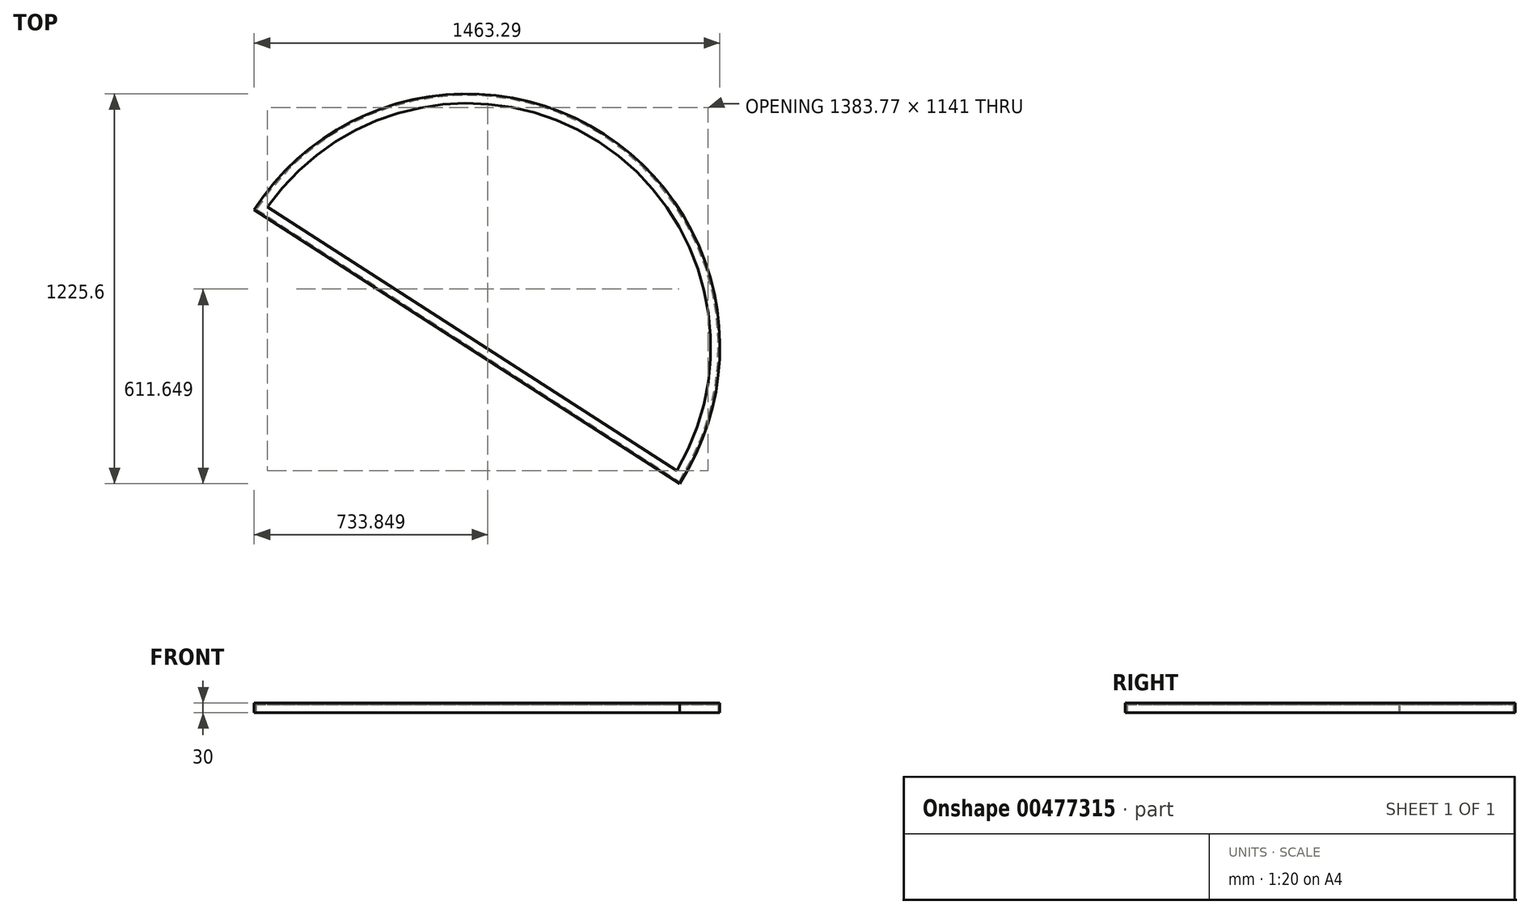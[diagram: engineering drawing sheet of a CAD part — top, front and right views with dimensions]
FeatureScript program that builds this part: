
annotation { "Feature Type Name" : "Feature", "Feature Type Description" : "" }
export const myFeature = defineFeature(function(context is Context, id is Id, definition is map)
    precondition{}
    {
        {
            var Q0;
            Q0=qCreatedBy(makeId("Top.planeOp"),FACE);
            var sketch = newSketch(context, id + "F0", { "sketchPlane" : qUnion([Q0])});
            skArc(sketch, "E0", {"start": v(668.29, -430.6) * mm, "mid": v(430.6, 668.29) * mm, "end": v(-668.29, 430.6) * mm});
            skArc(sketch, "E1", {"start": v(664.09, -427.9) * mm, "mid": v(427.9, 664.09) * mm, "end": v(-664.09, 427.9) * mm});
            skLineSegment(sketch, "E2", {"start": v(-668.29, 430.6) * mm, "end": v(0, 0) * mm});
            skLineSegment(sketch, "E3", {"start": v(0, 0) * mm, "end": v(668.29, -430.6) * mm});
            skLineSegment(sketch, "E4", {"start": v(-664.09, 433.84) * mm, "end": v(668.29, -424.65) * mm});
            skSolve(sketch);
        }
        {
            var Q0;
            Q0=makeQuery(id+"F0.imprint","IMPRINT",FACE,{"disambiguationData":[TD([[makeQuery(id+"F0.imprint","IMPRINT",EDGE,{"derivedFrom":sQuery(id+"F0.wireOp",EDGE,"E0")}),1.0]])]});
            var Q1;
            {var subQ1=sQuery(id+"F0.wireOp",EDGE,"E1");var subQ3=sQuery(id+"F0.wireOp",EDGE,"E3");var subQ7=makeQuery(id+"F0.imprint","INTERSECT",VERTEX,{"derivedFrom":[subQ1,subQ3]});Q1=makeQuery(id+"F0.imprint","IMPRINT",FACE,{"disambiguationData":[TD([[makeQuery(id+"F0.imprint","IMPRINT",EDGE,{"disambiguationData":[TD([[subQ7,-1.0]])],"derivedFrom":subQ1}),1.0]])]});}
            var Q2;
            {var subQ0=sQuery(id+"F0.wireOp",EDGE,"E3");var subQ1=sQuery(id+"F0.wireOp",EDGE,"E0");var subQ2=makeQuery(id+"F0.imprint","INTERSECT",VERTEX,{"derivedFrom":[subQ1,subQ0]});Q2=makeQuery(id+"F0.imprint","IMPRINT",FACE,{"disambiguationData":[TD([[makeQuery(id+"F0.imprint","IMPRINT",EDGE,{"disambiguationData":[TD([[subQ2,-1.0]])],"derivedFrom":subQ1}),1.0]])]});}
            extrude(context, id + "F1", {"entities" : qUnion([Q0, Q1, Q2]), "endBound" : BoundingType.SYMMETRIC, "oppositeDirection" : true, "depth" : 25 * mm});
        }
        {
            var Q0;
            Q0=makeQuery(id+"F1.opExtrude","CAP_FACE",FACE,{"disambiguationData":[OSD([sQuery(id+"F0.wireOp",EDGE,"E0"),sQuery(id+"F0.wireOp",EDGE,"E1"),sQuery(id+"F0.wireOp",EDGE,"E2"),sQuery(id+"F0.wireOp",EDGE,"E3"),sQuery(id+"F0.wireOp",EDGE,"E4")])],"isStart":true});
            var sketch = newSketch(context, id + "F2", { "sketchPlane" : qUnion([Q0])});
            skLineSegment(sketch, "E5.0", {"start": v(-668.29, 430.6) * mm, "end": v(668.29, -430.6) * mm});
            skArc(sketch, "E6.0", {"start": v(668.29, -430.6) * mm, "mid": v(430.6, 668.29) * mm, "end": v(-668.29, 430.6) * mm});
            skLineSegment(sketch, "E7", {"start": v(-642.99, 449.98) * mm, "end": v(670.8, -396.53) * mm});
            skSolve(sketch);
        }
        {
            var Q0;
            Q0=makeQuery(id+"F1.opExtrude","CAP_FACE",FACE,{"disambiguationData":[OSD([sQuery(id+"F0.wireOp",EDGE,"E0"),sQuery(id+"F0.wireOp",EDGE,"E1"),sQuery(id+"F0.wireOp",EDGE,"E2"),sQuery(id+"F0.wireOp",EDGE,"E3"),sQuery(id+"F0.wireOp",EDGE,"E4")])],"isStart":true});
            var sketch = newSketch(context, id + "F3", { "sketchPlane" : qUnion([Q0])});
            skArc(sketch, "E8.0", {"start": v(668.29, -430.6) * mm, "mid": v(430.6, 668.29) * mm, "end": v(-668.29, 430.6) * mm});
            skLineSegment(sketch, "E9.0", {"start": v(-668.29, 430.6) * mm, "end": v(668.29, -430.6) * mm});
            skLineSegment(sketch, "E10", {"start": v(-626.33, 439.25) * mm, "end": v(659.81, -389.45) * mm});
            skArc(sketch, "E11", {"start": v(659.81, -389.45) * mm, "mid": v(415.15, 643.23) * mm, "end": v(-626.33, 439.25) * mm});
            skSolve(sketch);
        }
        {
            var Q0;
            Q0=makeQuery(id+"F3.imprint","IMPRINT",FACE,{"disambiguationData":[TD([[makeQuery(id+"F3.imprint","IMPRINT",EDGE,{"derivedFrom":sQuery(id+"F3.wireOp",EDGE,"E10")}),-1.0]])]});
            var Q1;
            Q1=makeQuery(id+"F2.imprint","IMPRINT",FACE,{"disambiguationData":[TD([[makeQuery(id+"F2.imprint","IMPRINT",EDGE,{"derivedFrom":sQuery(id+"F2.wireOp",EDGE,"E5.0")}),1.0]])]});
            extrude(context, id + "F4", {"entities" : qUnion([Q0, Q1]), "operationType" : NewBodyOperationType.ADD, "depth" : 5 * mm});
        }
    });
